# Revit family: Tub_Filler-DXV-Fitzgerald-D35160950_Series
name_source: partatom
category: Plumbing Fixtures
revit_build: Autodesk Revit 2014 (Build: 20130308_1515(x64)
units: mm (PartAtom-declared; Revit-internal decimal feet)

## types (3) — shared parameters
ADA Compliant = Yes
Assembly Code = D2020300
CW Connection = Yes
CWFU = 3
Cold Water Connection Diameter = 1/2"
Cold Water Connection Radius = 1/4"
Cold Water Connection Width = 3"
Default Elevation = 0"
Description = Fitzgerald Floor Mount Tub Filler
Flow Rate = 1.8 gpm (6.8 L/min)
HW Connection = Yes
HWFU = 3
Height = 29 13/16"
Hot Water Connection Diameter = 1"
Hot Water Connection Radius = 1/4"
Hot Water Connection Width = 3"
Installation Type = Floor Mounted
Length = 11 5/8"
Manufacturer = DXV
Price = Prices may vary. Please consult Manufacturer Representative for most up-to-date price list.
Product Documentation Link = https://dxv01.blob.core.windows.net
Product Page URL = https://www.dxv.com
URL = http://www.dxv.com
Vent Connection = No
WFU = 4
Warranty Documentation Link = https://www.dxv.com
Waste Connection = No
Width = 12 5/8"

## per-type parameters (varying)
| type | Finish | Material |
| D35160950.100 | Metal-DXV-100-Polished Chrome | Metal-DXV-100-Polished Chrome |
| D35160950.144 | Metal-DXV-144-Brushed Nickel | Metal-DXV-144-Brushed Nickel |
| D35160950.150 | Metal-DXV-150-Platinum Nickel | Metal-DXV-150-Platinum Nickel |

note: column(s) folded — value = type name in every type: Model
